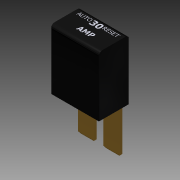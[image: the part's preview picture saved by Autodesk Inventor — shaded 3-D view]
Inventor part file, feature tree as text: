
AUTODESK INVENTOR PART (.ipt)
format: ipt  version: 2013 (Build 170138000, 138)  size: 480,256 bytes
history: native  units: in
note: dims shown in document units (in); Inventor stores cm internally (conversion verified against a paired STEP export)
features: sketch x6, extrude x4, plane x3, emboss x2, fillet x1, mirror x1
ambient origin geometry x8: Origin, YZ Plane, XZ Plane, XY Plane, X Axis, Y Axis, Z Axis, Center Point
bodies: Solid1 (feature_tree)
feature tree (17):
  extrude  "Extrusion1"  Depth=0.39in
  fillet  "Fillet1"  Radius=0.78in
  extrude  "Extrusion3"  Depth=0.212in
  extrude  "Extrusion4"  Depth=0.0585in
  extrude  "Extrusion5"  Depth=0.57in TaperAngle=0.0deg
  plane  "Work Plane1"
  mirror  "Mirror1"
  plane  "Work Plane2"
  emboss  "Emboss1"
  plane  "Work Plane4"
  emboss  "Emboss3"
  sketch  "Sketch1"  dims[d0=0.62in d1=0.39in d2=0.78in d3=0.0in]
  sketch  "Sketch2"  dims[d4=0.01in d5=0.05in d6=0.212in]
  sketch  "Sketch3"  dims[d8=0.031in d13=0.0585in]
  sketch  "Sketch4"  dims[d14=0.57in d15=0.0in d16=0.57in d17=0.0in]
  sketch  "Sketch6"  dims[d18=0.023in]
  sketch  "Sketch8"  dims[d19=0.023in d20=0.023in d21=0.57in d22=0.0in d26=0.1875in d27=0.0001in d28=0.0in d32=0.1875in d33=0.0001in d34=0.0in]
